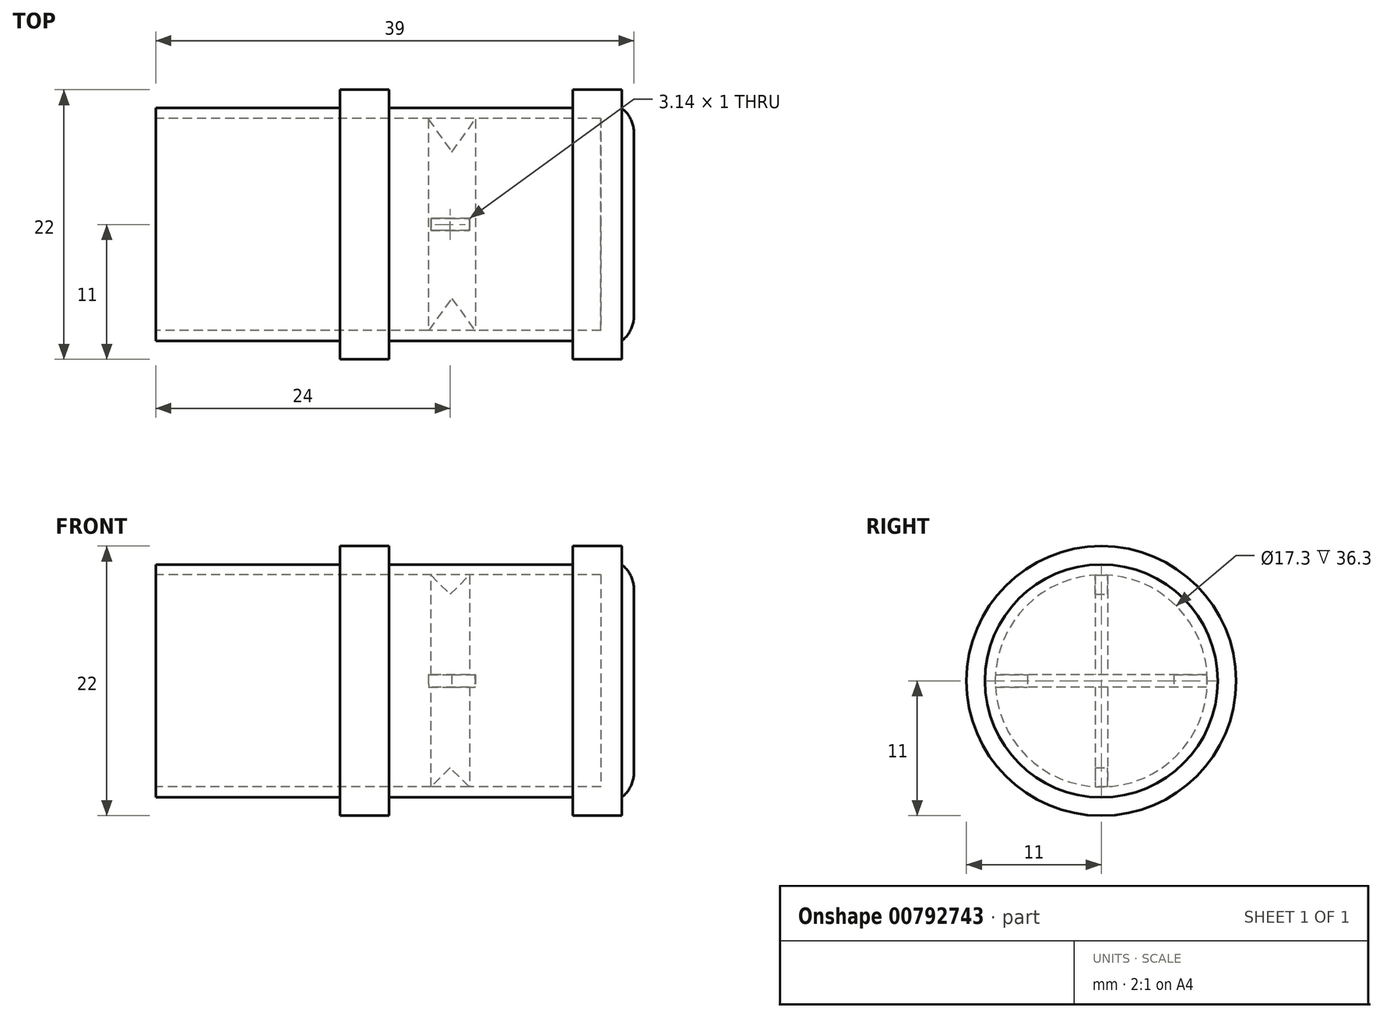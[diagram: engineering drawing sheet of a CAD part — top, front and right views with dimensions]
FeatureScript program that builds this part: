
annotation { "Feature Type Name" : "Feature", "Feature Type Description" : "" }
export const myFeature = defineFeature(function(context is Context, id is Id, definition is map)
    precondition{}
    {
        {
            var Q0;
            Q0=qCreatedBy(makeId("Right.planeOp"),FACE);
            var sketch = newSketch(context, id + "F0", { "sketchPlane" : qUnion([Q0])});
            skCircle(sketch, "E0", {"center": v(0, 0) * mm, "radius": 9.5 * mm});
            skSolve(sketch);
        }
        {
            var Q0;
            Q0=makeQuery(id+"F0.imprint","IMPRINT",FACE,{"disambiguationData":[TD([[makeQuery(id+"F0.imprint","IMPRINT",EDGE,{"derivedFrom":sQuery(id+"F0.wireOp",EDGE,"E0")}),1.0]])]});
            extrude(context, id + "F1", {"entities" : qUnion([Q0]), "depth" : 15 * mm, "offsetDistance" : 25 * mm});
        }
        {
            var Q0;
            Q0=makeQuery(id+"F1.opExtrude","CAP_FACE",FACE,{"disambiguationData":[OSD([sQuery(id+"F0.wireOp",EDGE,"E0")])],"isStart":false});
            var sketch = newSketch(context, id + "F2", { "sketchPlane" : qUnion([Q0])});
            skCircle(sketch, "E1", {"center": v(0, 0) * mm, "radius": 11 * mm});
            skSolve(sketch);
        }
        {
            var Q0;
            Q0 = qSketchRegion(id + "F2", true);
            extrude(context, id + "F3", {"entities" : qUnion([Q0]), "operationType" : NewBodyOperationType.ADD, "depth" : 4 * mm, "offsetDistance" : 25 * mm});
        }
        {
            var Q0;
            Q0=makeQuery(id+"F3.opExtrude","CAP_FACE",FACE,{"disambiguationData":[OSD([sQuery(id+"F2.wireOp",EDGE,"E1")])],"isStart":false});
            var sketch = newSketch(context, id + "F4", { "sketchPlane" : qUnion([Q0])});
            skCircle(sketch, "E2", {"center": v(0, 0) * mm, "radius": 9.5 * mm});
            skSolve(sketch);
        }
        {
            var Q0;
            Q0=makeQuery(id+"F4.imprint","IMPRINT",FACE,{"disambiguationData":[TD([[makeQuery(id+"F4.imprint","IMPRINT",EDGE,{"derivedFrom":sQuery(id+"F4.wireOp",EDGE,"E2")}),1.0]])]});
            extrude(context, id + "F5", {"entities" : qUnion([Q0]), "operationType" : NewBodyOperationType.ADD, "depth" : 15 * mm, "offsetDistance" : 25 * mm});
        }
        {
            var Q0;
            Q0=makeQuery(id+"F5.opExtrude","CAP_FACE",FACE,{"disambiguationData":[OSD([sQuery(id+"F4.wireOp",EDGE,"E2")])],"isStart":false});
            var sketch = newSketch(context, id + "F6", { "sketchPlane" : qUnion([Q0])});
            skCircle(sketch, "E3", {"center": v(0, 0) * mm, "radius": 11 * mm});
            skSolve(sketch);
        }
        {
            var Q0;
            Q0 = qSketchRegion(id + "F6", true);
            extrude(context, id + "F7", {"entities" : qUnion([Q0]), "operationType" : NewBodyOperationType.ADD, "depth" : 4 * mm, "offsetDistance" : 25 * mm});
        }
        {
            var Q0;
            Q0=makeQuery(id+"F7.opExtrude","CAP_FACE",FACE,{"disambiguationData":[OSD([sQuery(id+"F6.wireOp",EDGE,"E3")])],"isStart":false});
            var sketch = newSketch(context, id + "F8", { "sketchPlane" : qUnion([Q0])});
            skCircle(sketch, "E4", {"center": v(0, 0) * mm, "radius": 9.5 * mm});
            skSolve(sketch);
        }
        {
            var Q0;
            Q0=makeQuery(id+"F8.imprint","IMPRINT",FACE,{"disambiguationData":[TD([[makeQuery(id+"F8.imprint","IMPRINT",EDGE,{"derivedFrom":sQuery(id+"F8.wireOp",EDGE,"E4")}),1.0]])]});
            extrude(context, id + "F9", {"entities" : qUnion([Q0]), "operationType" : NewBodyOperationType.ADD, "depth" : 1 * mm, "offsetDistance" : 25 * mm});
        }
        {
            var Q0;
            Q0=makeQuery(id+"F9.opExtrude","CAP_FACE",FACE,{"disambiguationData":[OSD([sQuery(id+"F8.wireOp",EDGE,"E4")])],"isStart":false});
            fillet(context, id + "F10", {"entities" : qUnion([Q0]), "radius" : 2.66 * mm, "tangentPropagation" : true, "allowEdgeOverflow" : false});
        }
        {
            var Q0;
            Q0=makeQuery(id+"F1.opExtrude","CAP_FACE",FACE,{"disambiguationData":[OSD([sQuery(id+"F0.wireOp",EDGE,"E0")])],"isStart":true});
            var sketch = newSketch(context, id + "F11", { "sketchPlane" : qUnion([Q0])});
            skCircle(sketch, "E5", {"center": v(0, 0) * mm, "radius": 8.65 * mm});
            skSolve(sketch);
        }
        {
            var Q0;
            Q0=makeQuery(id+"F11.imprint","IMPRINT",FACE,{"disambiguationData":[TD([[makeQuery(id+"F11.imprint","IMPRINT",EDGE,{"derivedFrom":sQuery(id+"F11.wireOp",EDGE,"E5")}),1.0]])]});
            extrude(context, id + "F12", {"entities" : qUnion([Q0]), "operationType" : NewBodyOperationType.REMOVE, "oppositeDirection" : true, "depth" : 36.3 * mm, "offsetDistance" : 25 * mm});
        }
        {
            var Q0;
            Q0=qCreatedBy(makeId("Top.planeOp"),FACE);
            var sketch = newSketch(context, id + "F13", { "sketchPlane" : qUnion([Q0])});
            skLineSegment(sketch, "E6", {"start": v(22.23, 8.6) * mm, "end": v(22.23, -8.7) * mm});
            skLineSegment(sketch, "E7", {"start": v(26.06, 8.6) * mm, "end": v(26.06, -8.7) * mm});
            skLineSegment(sketch, "E8", {"start": v(22.23, 8.6) * mm, "end": v(24.14, 5.91) * mm});
            skLineSegment(sketch, "E9", {"start": v(24.14, 5.91) * mm, "end": v(26.06, 8.6) * mm});
            skLineSegment(sketch, "E10", {"start": v(22.23, -8.7) * mm, "end": v(24.14, -6.03) * mm});
            skLineSegment(sketch, "E11", {"start": v(24.14, -6.03) * mm, "end": v(26.06, -8.7) * mm});
            skSolve(sketch);
        }
        {
            var Q0;
            Q0=qCreatedBy(makeId("Front.planeOp"),FACE);
            var sketch = newSketch(context, id + "F14", { "sketchPlane" : qUnion([Q0])});
            skLineSegment(sketch, "E12", {"start": v(25.57, 8.64) * mm, "end": v(25.57, -8.66) * mm});
            skLineSegment(sketch, "E13", {"start": v(25.57, -8.66) * mm, "end": v(24, -7.09) * mm});
            skLineSegment(sketch, "E14", {"start": v(24, -7.09) * mm, "end": v(22.43, -8.66) * mm});
            skLineSegment(sketch, "E15", {"start": v(22.43, -8.66) * mm, "end": v(22.43, 8.64) * mm});
            skLineSegment(sketch, "E16", {"start": v(22.43, 8.64) * mm, "end": v(24, 7.07) * mm});
            skLineSegment(sketch, "E17", {"start": v(24, 7.07) * mm, "end": v(25.57, 8.64) * mm});
            skSolve(sketch);
        }
        {
            var Q0;
            Q0 = qSketchRegion(id + "F14", true);
            extrude(context, id + "F15", {"entities" : qUnion([Q0]), "operationType" : NewBodyOperationType.ADD, "endBound" : BoundingType.SYMMETRIC, "depth" : 1 * mm, "offsetDistance" : 25 * mm});
        }
        {
            var Q0;
            Q0 = qSketchRegion(id + "F13", true);
            extrude(context, id + "F16", {"entities" : qUnion([Q0]), "operationType" : NewBodyOperationType.ADD, "endBound" : BoundingType.SYMMETRIC, "depth" : 1 * mm, "offsetDistance" : 25 * mm});
        }
    });
